FCSTD DOCUMENT  (FreeCAD 0.20RUnknown)
Label: kato-r282-45
License: All rights reserved
LicenseURL: http://en.wikipedia.org/wiki/All_rights_reserved
objects: Sketcher::SketchObject×1, PartDesign::Body×1
note: 2 computed .brp shape members not serialized (recipe doc carries the construction recipe); baked Part::Feature solids carry a one-line shape summary decoded from their .brp

FEATURE [Sketcher::SketchObject] Sketch
  FullyConstrained = false
  MapMode = 5
  Support = -> [XY_Plane]
  sketch-geometry (3):
    g0: LineSegment StartX=0 StartY=0 StartZ=0 EndX=282 EndY=0 EndZ=0
    g1: LineSegment StartX=0 StartY=0 StartZ=0 EndX=199.404 EndY=199.404 EndZ=0
    g2: ArcOfCircle CenterX=0 CenterY=0 CenterZ=0 NormalX=0 NormalY=0 NormalZ=1 AngleXU=0 Radius=282 StartAngle=0 EndAngle=0.785398
  constraints (7):
    c: Coincident(g0,g-1)
    c: Horizontal(g0)
    c: DistanceX(g0,g0) = 282
    c: Coincident(g1,g0)
    c: Equal(g1,g0)
    c: Angle(g0,g1) = 0.785398
    c: Coincident(g2,g0)
FEATURE [PartDesign::Body] Body
  Group = -> [Sketch]
  Origin = -> Origin
